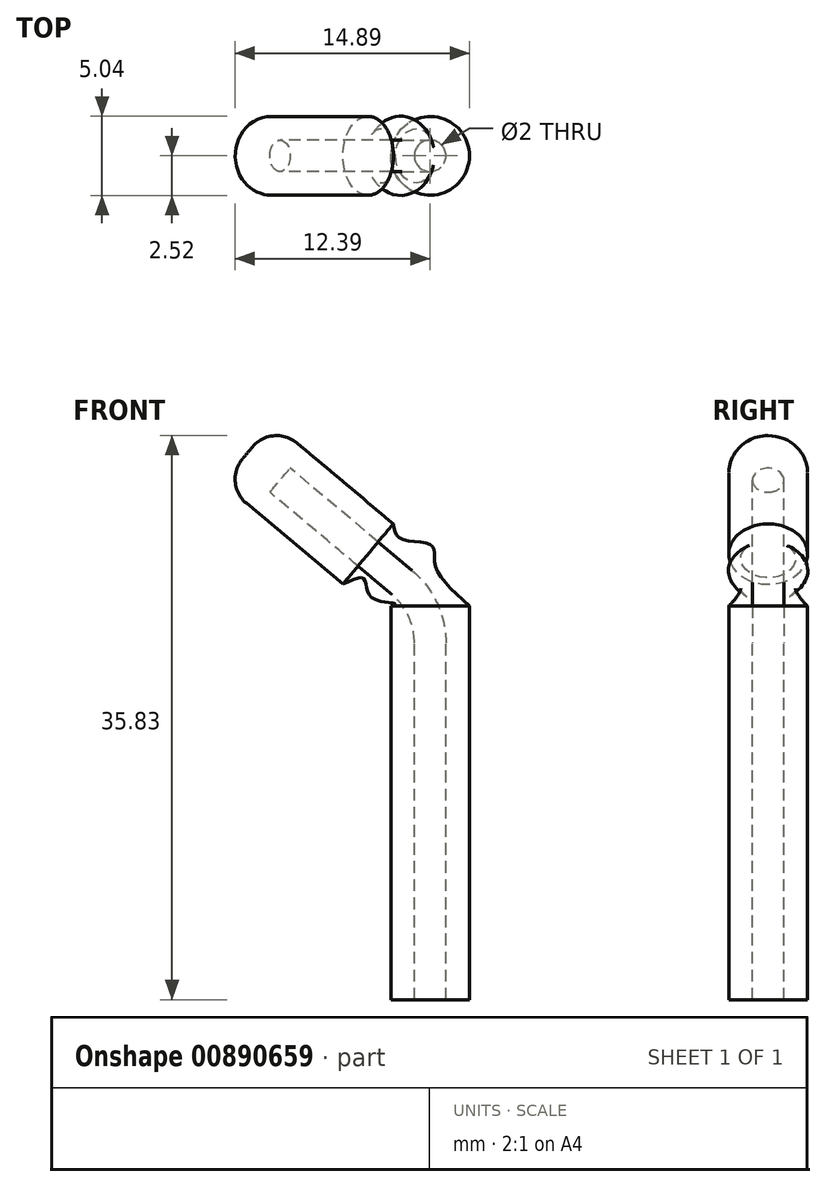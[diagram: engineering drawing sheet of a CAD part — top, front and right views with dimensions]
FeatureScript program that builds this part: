
annotation { "Feature Type Name" : "Feature", "Feature Type Description" : "" }
export const myFeature = defineFeature(function(context is Context, id is Id, definition is map)
    precondition{}
    {
        {
            var Q0;
            Q0=qCreatedBy(makeId("Top.planeOp"),FACE);
            var sketch = newSketch(context, id + "F0", { "sketchPlane" : qUnion([Q0])});
            skCircle(sketch, "E0", {"center": v(0, 0) * mm, "radius": 2.5 * mm});
            skSolve(sketch);
        }
        {
            var Q0;
            Q0=qCreatedBy(makeId("Top.planeOp"),FACE);
            cPlane(context, id + "F1", {"entities" : qUnion([Q0]), "cplaneType" : CPlaneType.OFFSET, "offset" : 2 * mm, "width" : 150 * mm, "height" : 150 * mm});
        }
        {
            var Q0;
            Q0=qCreatedBy(id+"F1.planeOp",FACE);
            var sketch = newSketch(context, id + "F2", { "sketchPlane" : qUnion([Q0])});
            skLineSegment(sketch, "E1", {"start": v(0, 5.6) * mm, "end": v(0, -3.44) * mm, "construction": true});
            skSolve(sketch);
        }
        {
            var Q0;
            Q0=sQuery(id+"F2.wireOp",EDGE,"E1");
            cPlane(context, id + "F3", {"entities" : qUnion([Q0]), "cplaneType" : CPlaneType.LINE_ANGLE, "offset" : 25 * mm, "angle" : 37.78 * degree, "width" : 150 * mm, "height" : 150 * mm});
        }
        {
            var Q0;
            Q0=qCreatedBy(id+"F1.planeOp",FACE);
            cPlane(context, id + "F4", {"entities" : qUnion([Q0]), "cplaneType" : CPlaneType.OFFSET, "offset" : 2 * mm, "width" : 150 * mm, "height" : 150 * mm});
        }
        {
            var Q0;
            Q0=qCreatedBy(id+"F4.planeOp",FACE);
            var sketch = newSketch(context, id + "F5", { "sketchPlane" : qUnion([Q0])});
            skLineSegment(sketch, "E2", {"start": v(0, 24.36) * mm, "end": v(0, -20.96) * mm, "construction": true});
            skSolve(sketch);
        }
        {
            var Q0;
            Q0=sQuery(id+"F5.wireOp",EDGE,"E2");
            cPlane(context, id + "F6", {"entities" : qUnion([Q0]), "cplaneType" : CPlaneType.LINE_ANGLE, "offset" : 25 * mm, "angle" : 40 * degree, "width" : 150 * mm, "height" : 150 * mm});
        }
        {
            var Q0;
            Q0=qCreatedBy(id+"F3.planeOp",FACE);
            var sketch = newSketch(context, id + "F7", { "sketchPlane" : qUnion([Q0])});
            skCircle(sketch, "E3", {"center": v(0, 0) * mm, "radius": 1.75 * mm});
            skSolve(sketch);
        }
        {
            var Q0;
            Q0=qCreatedBy(id+"F6.planeOp",FACE);
            var sketch = newSketch(context, id + "F8", { "sketchPlane" : qUnion([Q0])});
            skCircle(sketch, "E4", {"center": v(0, 0) * mm, "radius": 2.5 * mm});
            skSolve(sketch);
        }
        {
            var Q0;
            Q0=qCreatedBy(id+"F4.planeOp",FACE);
            cPlane(context, id + "F9", {"entities" : qUnion([Q0]), "cplaneType" : CPlaneType.OFFSET, "offset" : 2 * mm, "width" : 150 * mm, "height" : 150 * mm});
        }
        {
            var Q0;
            Q0=qCreatedBy(id+"F9.planeOp",FACE);
            var sketch = newSketch(context, id + "F10", { "sketchPlane" : qUnion([Q0])});
            skLineSegment(sketch, "E5", {"start": v(0, 17.98) * mm, "end": v(0, -15.31) * mm, "construction": true});
            skSolve(sketch);
        }
        {
            var Q0;
            Q0=sQuery(id+"F10.wireOp",EDGE,"E5");
            cPlane(context, id + "F11", {"entities" : qUnion([Q0]), "cplaneType" : CPlaneType.LINE_ANGLE, "offset" : 25 * mm, "angle" : 45 * degree, "width" : 150 * mm, "height" : 150 * mm});
        }
        {
            var Q0;
            Q0=qCreatedBy(id+"F11.planeOp",FACE);
            var sketch = newSketch(context, id + "F12", { "sketchPlane" : qUnion([Q0])});
            skCircle(sketch, "E6", {"center": v(0, 0) * mm, "radius": 1.75 * mm});
            skSolve(sketch);
        }
        {
            var Q0;
            Q0=qCreatedBy(id+"F9.planeOp",FACE);
            cPlane(context, id + "F13", {"entities" : qUnion([Q0]), "cplaneType" : CPlaneType.OFFSET, "offset" : 2 * mm, "width" : 150 * mm, "height" : 150 * mm});
        }
        {
            var Q0;
            Q0=qCreatedBy(id+"F13.planeOp",FACE);
            var sketch = newSketch(context, id + "F14", { "sketchPlane" : qUnion([Q0])});
            skLineSegment(sketch, "E7", {"start": v(0, 32.2) * mm, "end": v(0, -35.66) * mm, "construction": true});
            skSolve(sketch);
        }
        {
            var Q0;
            Q0=sQuery(id+"F14.wireOp",EDGE,"E7");
            cPlane(context, id + "F15", {"entities" : qUnion([Q0]), "cplaneType" : CPlaneType.LINE_ANGLE, "offset" : 25 * mm, "angle" : 50 * degree, "width" : 150 * mm, "height" : 150 * mm});
        }
        {
            var Q0;
            Q0=qCreatedBy(id+"F15.planeOp",FACE);
            var sketch = newSketch(context, id + "F16", { "sketchPlane" : qUnion([Q0])});
            skCircle(sketch, "E8", {"center": v(0, 0) * mm, "radius": 2.5 * mm});
            skSolve(sketch);
        }
        {
            var Q0;
            Q0=makeQuery(id+"F0.imprint","IMPRINT",FACE,{"disambiguationData":[TD([[makeQuery(id+"F0.imprint","IMPRINT",EDGE,{"derivedFrom":sQuery(id+"F0.wireOp",EDGE,"E0")}),1.0]])]});
            var Q1;
            Q1=sQuery(id+"F0.wireOp",EDGE,"E0");
            extrude(context, id + "F17", {"entities" : qUnion([Q0]), "surfaceEntities" : qUnion([Q1]), "oppositeDirection" : true, "depth" : 25 * mm, "offsetDistance" : 25 * mm});
        }
        {
            var Q0;
            Q0=makeQuery(id+"F17.opExtrude","CAP_FACE",FACE,{"disambiguationData":[OSD([sQuery(id+"F0.wireOp",EDGE,"E0")])],"isStart":true});
            var sketch = newSketch(context, id + "F18", { "sketchPlane" : qUnion([Q0])});
            skCircle(sketch, "E9", {"center": v(0, 0) * mm, "radius": 2.5 * mm});
            skSolve(sketch);
        }
        {
            var Q0;
            Q0=makeQuery(id+"F18.imprint","IMPRINT",FACE,{"disambiguationData":[TD([[makeQuery(id+"F18.imprint","IMPRINT",EDGE,{"derivedFrom":sQuery(id+"F18.wireOp",EDGE,"E9")}),1.0]])]});
            var Q1;
            Q1=makeQuery(id+"F7.imprint","IMPRINT",FACE,{"disambiguationData":[TD([[makeQuery(id+"F7.imprint","IMPRINT",EDGE,{"derivedFrom":sQuery(id+"F7.wireOp",EDGE,"E3")}),1.0]])]});
            var Q2;
            Q2=makeQuery(id+"F8.imprint","IMPRINT",FACE,{"disambiguationData":[TD([[makeQuery(id+"F8.imprint","IMPRINT",EDGE,{"derivedFrom":sQuery(id+"F8.wireOp",EDGE,"E4")}),1.0]])]});
            var Q3;
            Q3=makeQuery(id+"F12.imprint","IMPRINT",FACE,{"disambiguationData":[TD([[makeQuery(id+"F12.imprint","IMPRINT",EDGE,{"derivedFrom":sQuery(id+"F12.wireOp",EDGE,"E6")}),1.0]])]});
            var Q4;
            Q4=makeQuery(id+"F16.imprint","IMPRINT",FACE,{"disambiguationData":[TD([[makeQuery(id+"F16.imprint","IMPRINT",EDGE,{"derivedFrom":sQuery(id+"F16.wireOp",EDGE,"E8")}),1.0]])]});
            loft(context, id + "F19", {"operationType" : NewBodyOperationType.ADD, "sheetProfilesArray" : [{ "sheetProfileEntities" : qUnion([Q0]) }, { "sheetProfileEntities" : qUnion([Q1]) }, { "sheetProfileEntities" : qUnion([Q2]) }, { "sheetProfileEntities" : qUnion([Q3]) }, { "sheetProfileEntities" : qUnion([Q4]) }]});
        }
        {
            var Q0;
            Q0=makeQuery(id+"F19.opLoft","CAP_FACE",FACE,{"disambiguationData":[OSD([makeQuery(id+"F16.imprint","IMPRINT",FACE,{"disambiguationData":[TD([[makeQuery(id+"F16.imprint","IMPRINT",EDGE,{"derivedFrom":sQuery(id+"F16.wireOp",EDGE,"E8")}),1.0]])]})])],"isStart":true});
            extrude(context, id + "F20", {"entities" : qUnion([Q0]), "operationType" : NewBodyOperationType.ADD, "depth" : 10 * mm, "offsetDistance" : 25 * mm});
        }
        {
            var Q0;
            Q0=makeQuery(id+"F20.opExtrude","CAP_EDGE",EDGE,{"disambiguationData":[OSD([sQuery(id+"F16.wireOp",EDGE,"E8")])],"isStart":false});
            fillet(context, id + "F21", {"entities" : qUnion([Q0]), "radius" : 2 * mm, "tangentPropagation" : true, "allowEdgeOverflow" : false});
        }
        {
            var Q0;
            Q0=qCreatedBy(makeId("Front.planeOp"),FACE);
            var sketch = newSketch(context, id + "F22", { "sketchPlane" : qUnion([Q0])});
            skLineSegment(sketch, "E10", {"start": v(0, -25) * mm, "end": v(0, -2.33) * mm});
            skLineSegment(sketch, "E11", {"start": v(-1.79, 1.5) * mm, "end": v(-9.53, 8) * mm});
            skPoint(sketch, "E12.visualSharp", {"position": v(0, 0) * mm});
            skArc(sketch, "E12.filletArc", {"start": v(0, -2.33) * mm, "mid": v(-0.47, -0.22) * mm, "end": v(-1.79, 1.5) * mm});
            skSolve(sketch);
        }
        {
            var Q0;
            Q0=makeQuery(id+"F17.opExtrude","CAP_FACE",FACE,{"disambiguationData":[OSD([sQuery(id+"F0.wireOp",EDGE,"E0")])],"isStart":false});
            var sketch = newSketch(context, id + "F23", { "sketchPlane" : qUnion([Q0])});
            skCircle(sketch, "E13", {"center": v(0, 0) * mm, "radius": 1 * mm});
            skSolve(sketch);
        }
        {
            var Q0;
            Q0=makeQuery(id+"F23.imprint","IMPRINT",FACE,{"disambiguationData":[TD([[makeQuery(id+"F23.imprint","IMPRINT",EDGE,{"derivedFrom":sQuery(id+"F23.wireOp",EDGE,"E13")}),1.0]])]});
            var Q1;
            Q1=sQuery(id+"F22.wireOp",EDGE,"E10");
            var Q2;
            Q2=sQuery(id+"F22.wireOp",EDGE,"E12.filletArc");
            var Q3;
            Q3=sQuery(id+"F22.wireOp",EDGE,"E11");
            sweep(context, id + "F24", {"operationType" : NewBodyOperationType.REMOVE, "profiles" : qUnion([Q0]), "path" : qUnion([Q1, Q2, Q3])});
        }
    });
